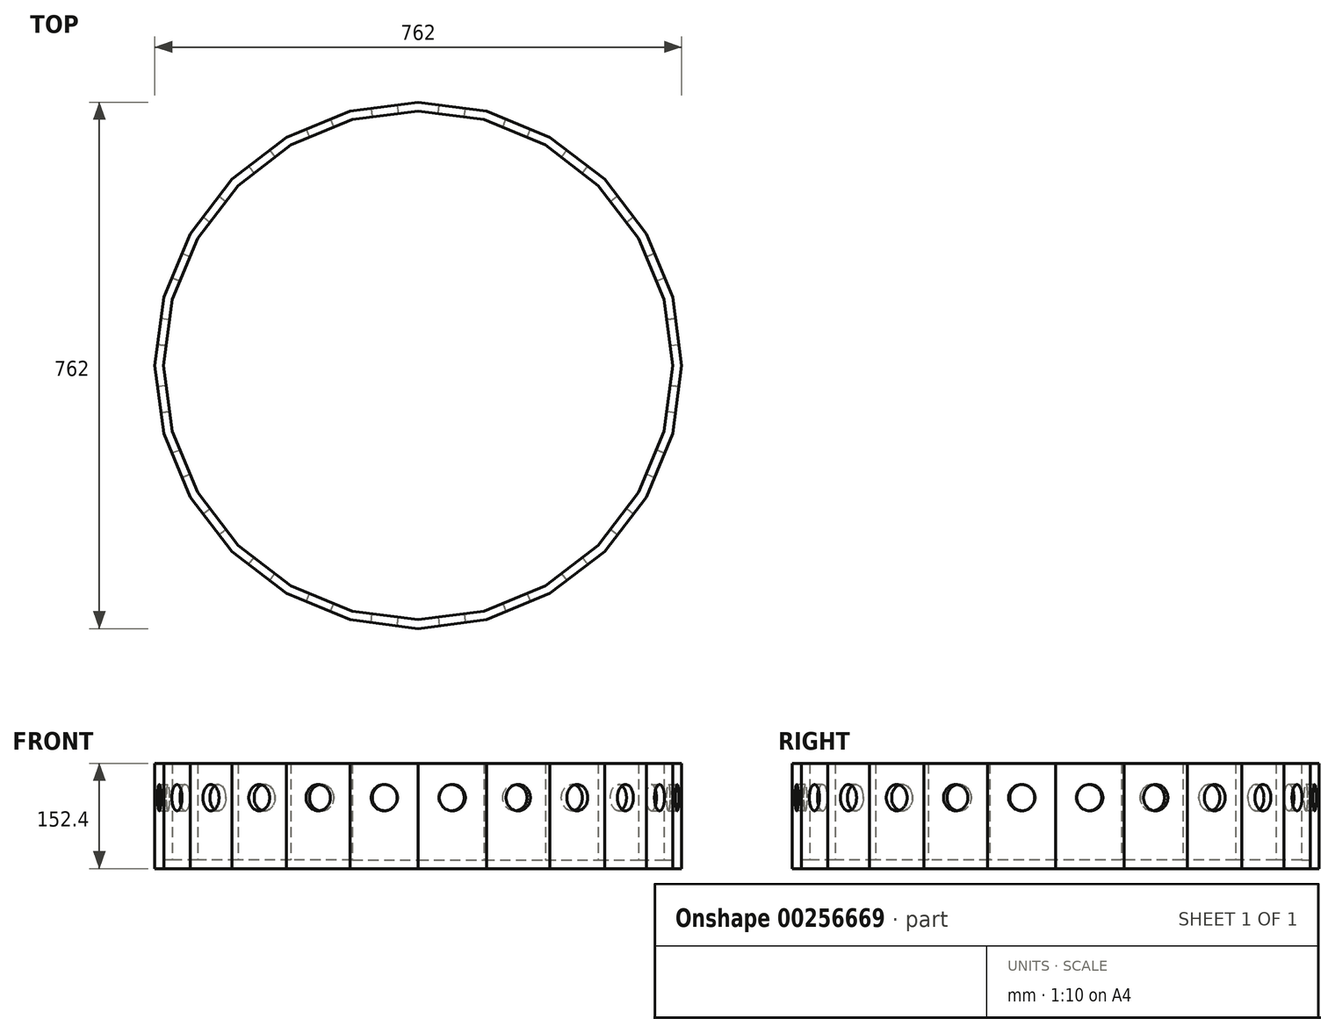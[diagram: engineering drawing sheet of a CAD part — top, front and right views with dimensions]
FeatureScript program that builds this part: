
annotation { "Feature Type Name" : "Feature", "Feature Type Description" : "" }
export const myFeature = defineFeature(function(context is Context, id is Id, definition is map)
    precondition{}
    {
        {
            var Q0;
            Q0=qCreatedBy(makeId("Top.planeOp"),FACE);
            var sketch = newSketch(context, id + "F0", { "sketchPlane" : qUnion([Q0])});
            skCircle(sketch, "E0.cCircle", {"center": v(0, 0) * mm, "radius": 381 * mm, "construction": true});
            skLineSegment(sketch, "E0.0", {"start": v(0, 381) * mm, "end": v(98.61, 368.02) * mm});
            skLineSegment(sketch, "E0.1", {"start": v(98.61, 368.02) * mm, "end": v(190.5, 329.96) * mm});
            skLineSegment(sketch, "E0.2", {"start": v(190.5, 329.96) * mm, "end": v(269.4, 269.4) * mm});
            skLineSegment(sketch, "E0.3", {"start": v(269.4, 269.4) * mm, "end": v(329.96, 190.5) * mm});
            skLineSegment(sketch, "E0.4", {"start": v(329.96, 190.5) * mm, "end": v(368.02, 98.61) * mm});
            skLineSegment(sketch, "E0.5", {"start": v(368.02, 98.61) * mm, "end": v(381, 0) * mm});
            skLineSegment(sketch, "E0.6", {"start": v(381, 0) * mm, "end": v(368.02, -98.61) * mm});
            skLineSegment(sketch, "E0.7", {"start": v(368.02, -98.61) * mm, "end": v(329.96, -190.5) * mm});
            skLineSegment(sketch, "E0.8", {"start": v(329.96, -190.5) * mm, "end": v(269.4, -269.4) * mm});
            skLineSegment(sketch, "E0.9", {"start": v(269.4, -269.4) * mm, "end": v(190.5, -329.96) * mm});
            skLineSegment(sketch, "E0.10", {"start": v(190.5, -329.96) * mm, "end": v(98.61, -368.02) * mm});
            skLineSegment(sketch, "E0.11", {"start": v(98.61, -368.02) * mm, "end": v(0, -381) * mm});
            skLineSegment(sketch, "E0.12", {"start": v(0, -381) * mm, "end": v(-98.61, -368.02) * mm});
            skLineSegment(sketch, "E0.13", {"start": v(-98.61, -368.02) * mm, "end": v(-190.5, -329.96) * mm});
            skLineSegment(sketch, "E0.14", {"start": v(-190.5, -329.96) * mm, "end": v(-269.4, -269.4) * mm});
            skLineSegment(sketch, "E0.15", {"start": v(-269.4, -269.4) * mm, "end": v(-329.96, -190.5) * mm});
            skLineSegment(sketch, "E0.16", {"start": v(-329.96, -190.5) * mm, "end": v(-368.02, -98.61) * mm});
            skLineSegment(sketch, "E0.17", {"start": v(-368.02, -98.61) * mm, "end": v(-381, 0) * mm});
            skLineSegment(sketch, "E0.18", {"start": v(-381, 0) * mm, "end": v(-368.02, 98.61) * mm});
            skLineSegment(sketch, "E0.19", {"start": v(-368.02, 98.61) * mm, "end": v(-329.96, 190.5) * mm});
            skLineSegment(sketch, "E0.20", {"start": v(-329.96, 190.5) * mm, "end": v(-269.4, 269.4) * mm});
            skLineSegment(sketch, "E0.21", {"start": v(-269.4, 269.4) * mm, "end": v(-190.5, 329.96) * mm});
            skLineSegment(sketch, "E0.22", {"start": v(-190.5, 329.96) * mm, "end": v(-98.61, 368.02) * mm});
            skLineSegment(sketch, "E0.23", {"start": v(-98.61, 368.02) * mm, "end": v(0, 381) * mm});
            skCircle(sketch, "E1.cCircle", {"center": v(0, 0) * mm, "radius": 368.2 * mm, "construction": true});
            skLineSegment(sketch, "E1.0", {"start": v(0, 368.2) * mm, "end": v(95.3, 355.64) * mm});
            skLineSegment(sketch, "E1.1", {"start": v(95.3, 355.64) * mm, "end": v(184.1, 318.86) * mm});
            skLineSegment(sketch, "E1.2", {"start": v(184.1, 318.86) * mm, "end": v(260.35, 260.35) * mm});
            skLineSegment(sketch, "E1.3", {"start": v(260.35, 260.35) * mm, "end": v(318.86, 184.1) * mm});
            skLineSegment(sketch, "E1.4", {"start": v(318.86, 184.1) * mm, "end": v(355.64, 95.3) * mm});
            skLineSegment(sketch, "E1.5", {"start": v(355.64, 95.3) * mm, "end": v(368.2, 0) * mm});
            skLineSegment(sketch, "E1.6", {"start": v(368.2, 0) * mm, "end": v(355.64, -95.3) * mm});
            skLineSegment(sketch, "E1.7", {"start": v(355.64, -95.3) * mm, "end": v(318.86, -184.1) * mm});
            skLineSegment(sketch, "E1.8", {"start": v(318.86, -184.1) * mm, "end": v(260.35, -260.35) * mm});
            skLineSegment(sketch, "E1.9", {"start": v(260.35, -260.35) * mm, "end": v(184.1, -318.86) * mm});
            skLineSegment(sketch, "E1.10", {"start": v(184.1, -318.86) * mm, "end": v(95.3, -355.64) * mm});
            skLineSegment(sketch, "E1.11", {"start": v(95.3, -355.64) * mm, "end": v(0, -368.2) * mm});
            skLineSegment(sketch, "E1.12", {"start": v(0, -368.2) * mm, "end": v(-95.3, -355.64) * mm});
            skLineSegment(sketch, "E1.13", {"start": v(-95.3, -355.64) * mm, "end": v(-184.1, -318.86) * mm});
            skLineSegment(sketch, "E1.14", {"start": v(-184.1, -318.86) * mm, "end": v(-260.35, -260.35) * mm});
            skLineSegment(sketch, "E1.15", {"start": v(-260.35, -260.35) * mm, "end": v(-318.86, -184.1) * mm});
            skLineSegment(sketch, "E1.16", {"start": v(-318.86, -184.1) * mm, "end": v(-355.64, -95.3) * mm});
            skLineSegment(sketch, "E1.17", {"start": v(-355.64, -95.3) * mm, "end": v(-368.2, 0) * mm});
            skLineSegment(sketch, "E1.18", {"start": v(-368.2, 0) * mm, "end": v(-355.64, 95.3) * mm});
            skLineSegment(sketch, "E1.19", {"start": v(-355.64, 95.3) * mm, "end": v(-318.86, 184.1) * mm});
            skLineSegment(sketch, "E1.20", {"start": v(-318.86, 184.1) * mm, "end": v(-260.35, 260.35) * mm});
            skLineSegment(sketch, "E1.21", {"start": v(-260.35, 260.35) * mm, "end": v(-184.1, 318.86) * mm});
            skLineSegment(sketch, "E1.22", {"start": v(-184.1, 318.86) * mm, "end": v(-95.3, 355.64) * mm});
            skLineSegment(sketch, "E1.23", {"start": v(-95.3, 355.64) * mm, "end": v(0, 368.2) * mm});
            skSolve(sketch);
        }
        {
            var Q0;
            Q0=makeQuery(id+"F0.imprint","IMPRINT",FACE,{"disambiguationData":[TD([[makeQuery(id+"F0.imprint","IMPRINT",EDGE,{"derivedFrom":sQuery(id+"F0.wireOp",EDGE,"E0.0")}),-1.0]])]});
            extrude(context, id + "F1", {"entities" : qUnion([Q0]), "depth" : 152.4 * mm});
        }
        {
            var Q0;
            Q0=makeQuery(id+"F0.imprint","IMPRINT",FACE,{"disambiguationData":[TD([[makeQuery(id+"F0.imprint","IMPRINT",EDGE,{"derivedFrom":sQuery(id+"F0.wireOp",EDGE,"E1.0")}),-1.0]])]});
            extrude(context, id + "F2", {"entities" : qUnion([Q0]), "operationType" : NewBodyOperationType.ADD, "depth" : 12.7 * mm});
        }
        {
            var Q0;
            Q0=makeQuery(id+"F1.opExtrude","SWEPT_FACE",FACE,{"disambiguationData":[OSD([sQuery(id+"F0.wireOp",EDGE,"E0.11")])]});
            var sketch = newSketch(context, id + "F3", { "sketchPlane" : qUnion([Q0])});
            skLineSegment(sketch, "E2.bottom", {"start": v(-49.73, 152.4) * mm, "end": v(49.73, 152.4) * mm});
            skLineSegment(sketch, "E2.top", {"start": v(-49.73, 52.94) * mm, "end": v(49.73, 52.94) * mm});
            skLineSegment(sketch, "E2.left", {"start": v(-49.73, 152.4) * mm, "end": v(-49.73, 52.94) * mm});
            skLineSegment(sketch, "E2.right", {"start": v(49.73, 152.4) * mm, "end": v(49.73, 52.94) * mm});
            skLineSegment(sketch, "E3", {"start": v(-49.73, 152.4) * mm, "end": v(49.73, 52.94) * mm});
            skPoint(sketch, "E4", {"position": v(0, 102.67) * mm});
            skSolve(sketch);
        }
        {
            var Q0;
            Q0=makeQuery(id+"F1.opExtrude","SWEPT_FACE",FACE,{"disambiguationData":[OSD([sQuery(id+"F0.wireOp",EDGE,"E0.10")])]});
            var sketch = newSketch(context, id + "F4", { "sketchPlane" : qUnion([Q0])});
            skLineSegment(sketch, "E5.bottom", {"start": v(-49.73, 152.4) * mm, "end": v(49.73, 152.4) * mm});
            skLineSegment(sketch, "E5.top", {"start": v(-49.73, 52.94) * mm, "end": v(49.73, 52.94) * mm});
            skLineSegment(sketch, "E5.left", {"start": v(-49.73, 152.4) * mm, "end": v(-49.73, 52.94) * mm});
            skLineSegment(sketch, "E5.right", {"start": v(49.73, 152.4) * mm, "end": v(49.73, 52.94) * mm});
            skLineSegment(sketch, "E6", {"start": v(-49.73, 152.4) * mm, "end": v(49.73, 52.94) * mm});
            skPoint(sketch, "E7", {"position": v(0, 102.67) * mm});
            skSolve(sketch);
        }
        {
            var Q0;
            Q0=makeQuery(id+"F1.opExtrude","SWEPT_FACE",FACE,{"disambiguationData":[OSD([sQuery(id+"F0.wireOp",EDGE,"E0.9")])]});
            var sketch = newSketch(context, id + "F5", { "sketchPlane" : qUnion([Q0])});
            skLineSegment(sketch, "E8.bottom", {"start": v(-49.73, 152.4) * mm, "end": v(49.73, 152.4) * mm});
            skLineSegment(sketch, "E8.top", {"start": v(-49.73, 52.94) * mm, "end": v(49.73, 52.94) * mm});
            skLineSegment(sketch, "E8.left", {"start": v(-49.73, 152.4) * mm, "end": v(-49.73, 52.94) * mm});
            skLineSegment(sketch, "E8.right", {"start": v(49.73, 152.4) * mm, "end": v(49.73, 52.94) * mm});
            skLineSegment(sketch, "E9", {"start": v(-49.73, 152.4) * mm, "end": v(49.73, 52.94) * mm});
            skPoint(sketch, "E10", {"position": v(0, 102.67) * mm});
            skSolve(sketch);
        }
        {
            var Q0;
            Q0=makeQuery(id+"F1.opExtrude","SWEPT_FACE",FACE,{"disambiguationData":[OSD([sQuery(id+"F0.wireOp",EDGE,"E0.8")])]});
            var sketch = newSketch(context, id + "F6", { "sketchPlane" : qUnion([Q0])});
            skLineSegment(sketch, "E11.bottom", {"start": v(-49.73, 152.4) * mm, "end": v(49.73, 152.4) * mm});
            skLineSegment(sketch, "E11.top", {"start": v(-49.73, 52.94) * mm, "end": v(49.73, 52.94) * mm});
            skLineSegment(sketch, "E11.left", {"start": v(-49.73, 152.4) * mm, "end": v(-49.73, 52.94) * mm});
            skLineSegment(sketch, "E11.right", {"start": v(49.73, 152.4) * mm, "end": v(49.73, 52.94) * mm});
            skLineSegment(sketch, "E12", {"start": v(-49.73, 152.4) * mm, "end": v(49.73, 52.94) * mm});
            skPoint(sketch, "E13", {"position": v(0, 102.67) * mm});
            skSolve(sketch);
        }
        {
            var Q0;
            Q0=makeQuery(id+"F1.opExtrude","SWEPT_FACE",FACE,{"disambiguationData":[OSD([sQuery(id+"F0.wireOp",EDGE,"E0.7")])]});
            var sketch = newSketch(context, id + "F7", { "sketchPlane" : qUnion([Q0])});
            skLineSegment(sketch, "E14.bottom", {"start": v(-49.73, 152.4) * mm, "end": v(49.73, 152.4) * mm});
            skLineSegment(sketch, "E14.top", {"start": v(-49.73, 52.94) * mm, "end": v(49.73, 52.94) * mm});
            skLineSegment(sketch, "E14.left", {"start": v(-49.73, 152.4) * mm, "end": v(-49.73, 52.94) * mm});
            skLineSegment(sketch, "E14.right", {"start": v(49.73, 152.4) * mm, "end": v(49.73, 52.94) * mm});
            skLineSegment(sketch, "E15", {"start": v(-49.73, 152.4) * mm, "end": v(49.73, 52.94) * mm});
            skPoint(sketch, "E16", {"position": v(0, 102.67) * mm});
            skSolve(sketch);
        }
        {
            var Q0;
            Q0=makeQuery(id+"F1.opExtrude","SWEPT_FACE",FACE,{"disambiguationData":[OSD([sQuery(id+"F0.wireOp",EDGE,"E0.6")])]});
            var sketch = newSketch(context, id + "F8", { "sketchPlane" : qUnion([Q0])});
            skLineSegment(sketch, "E17.bottom", {"start": v(-49.73, 152.4) * mm, "end": v(49.73, 152.4) * mm});
            skLineSegment(sketch, "E17.top", {"start": v(-49.73, 52.94) * mm, "end": v(49.73, 52.94) * mm});
            skLineSegment(sketch, "E17.left", {"start": v(-49.73, 152.4) * mm, "end": v(-49.73, 52.94) * mm});
            skLineSegment(sketch, "E17.right", {"start": v(49.73, 152.4) * mm, "end": v(49.73, 52.94) * mm});
            skLineSegment(sketch, "E18", {"start": v(-49.73, 152.4) * mm, "end": v(49.73, 52.94) * mm});
            skPoint(sketch, "E19", {"position": v(0, 102.67) * mm});
            skSolve(sketch);
        }
        {
            var Q0;
            Q0=makeQuery(id+"F1.opExtrude","SWEPT_FACE",FACE,{"disambiguationData":[OSD([sQuery(id+"F0.wireOp",EDGE,"E0.5")])]});
            var sketch = newSketch(context, id + "F9", { "sketchPlane" : qUnion([Q0])});
            skLineSegment(sketch, "E20.bottom", {"start": v(-49.73, 152.4) * mm, "end": v(49.73, 152.4) * mm});
            skLineSegment(sketch, "E20.top", {"start": v(-49.73, 52.94) * mm, "end": v(49.73, 52.94) * mm});
            skLineSegment(sketch, "E20.left", {"start": v(-49.73, 152.4) * mm, "end": v(-49.73, 52.94) * mm});
            skLineSegment(sketch, "E20.right", {"start": v(49.73, 152.4) * mm, "end": v(49.73, 52.94) * mm});
            skLineSegment(sketch, "E21", {"start": v(-49.73, 152.4) * mm, "end": v(49.73, 52.94) * mm});
            skPoint(sketch, "E22", {"position": v(0, 102.67) * mm});
            skSolve(sketch);
        }
        {
            var Q0;
            Q0=makeQuery(id+"F1.opExtrude","SWEPT_FACE",FACE,{"disambiguationData":[OSD([sQuery(id+"F0.wireOp",EDGE,"E0.4")])]});
            var sketch = newSketch(context, id + "F10", { "sketchPlane" : qUnion([Q0])});
            skLineSegment(sketch, "E23.bottom", {"start": v(-49.73, 152.4) * mm, "end": v(49.73, 152.4) * mm});
            skLineSegment(sketch, "E23.top", {"start": v(-49.73, 52.94) * mm, "end": v(49.73, 52.94) * mm});
            skLineSegment(sketch, "E23.left", {"start": v(-49.73, 152.4) * mm, "end": v(-49.73, 52.94) * mm});
            skLineSegment(sketch, "E23.right", {"start": v(49.73, 152.4) * mm, "end": v(49.73, 52.94) * mm});
            skLineSegment(sketch, "E24", {"start": v(-49.73, 152.4) * mm, "end": v(49.73, 52.94) * mm});
            skPoint(sketch, "E25", {"position": v(0, 102.67) * mm});
            skSolve(sketch);
        }
        {
            var Q0;
            Q0=makeQuery(id+"F1.opExtrude","SWEPT_FACE",FACE,{"disambiguationData":[OSD([sQuery(id+"F0.wireOp",EDGE,"E0.3")])]});
            var sketch = newSketch(context, id + "F11", { "sketchPlane" : qUnion([Q0])});
            skLineSegment(sketch, "E26.bottom", {"start": v(-49.73, 152.4) * mm, "end": v(49.73, 152.4) * mm});
            skLineSegment(sketch, "E26.top", {"start": v(-49.73, 52.94) * mm, "end": v(49.73, 52.94) * mm});
            skLineSegment(sketch, "E26.left", {"start": v(-49.73, 152.4) * mm, "end": v(-49.73, 52.94) * mm});
            skLineSegment(sketch, "E26.right", {"start": v(49.73, 152.4) * mm, "end": v(49.73, 52.94) * mm});
            skLineSegment(sketch, "E27", {"start": v(-49.73, 152.4) * mm, "end": v(49.73, 52.94) * mm});
            skPoint(sketch, "E28", {"position": v(0, 102.67) * mm});
            skSolve(sketch);
        }
        {
            var Q0;
            Q0=makeQuery(id+"F1.opExtrude","SWEPT_FACE",FACE,{"disambiguationData":[OSD([sQuery(id+"F0.wireOp",EDGE,"E0.2")])]});
            var sketch = newSketch(context, id + "F12", { "sketchPlane" : qUnion([Q0])});
            skLineSegment(sketch, "E29.bottom", {"start": v(-49.73, 152.4) * mm, "end": v(49.73, 152.4) * mm});
            skLineSegment(sketch, "E29.top", {"start": v(-49.73, 52.94) * mm, "end": v(49.73, 52.94) * mm});
            skLineSegment(sketch, "E29.left", {"start": v(-49.73, 152.4) * mm, "end": v(-49.73, 52.94) * mm});
            skLineSegment(sketch, "E29.right", {"start": v(49.73, 152.4) * mm, "end": v(49.73, 52.94) * mm});
            skLineSegment(sketch, "E30", {"start": v(-49.73, 152.4) * mm, "end": v(49.73, 52.94) * mm});
            skPoint(sketch, "E31", {"position": v(0, 102.67) * mm});
            skSolve(sketch);
        }
        {
            var Q0;
            Q0=makeQuery(id+"F1.opExtrude","SWEPT_FACE",FACE,{"disambiguationData":[OSD([sQuery(id+"F0.wireOp",EDGE,"E0.1")])]});
            var sketch = newSketch(context, id + "F13", { "sketchPlane" : qUnion([Q0])});
            skLineSegment(sketch, "E32.bottom", {"start": v(-49.73, 152.4) * mm, "end": v(49.73, 152.4) * mm});
            skLineSegment(sketch, "E32.top", {"start": v(-49.73, 52.94) * mm, "end": v(49.73, 52.94) * mm});
            skLineSegment(sketch, "E32.left", {"start": v(-49.73, 152.4) * mm, "end": v(-49.73, 52.94) * mm});
            skLineSegment(sketch, "E32.right", {"start": v(49.73, 152.4) * mm, "end": v(49.73, 52.94) * mm});
            skLineSegment(sketch, "E33", {"start": v(-49.73, 152.4) * mm, "end": v(49.73, 52.94) * mm});
            skPoint(sketch, "E34", {"position": v(0, 102.67) * mm});
            skSolve(sketch);
        }
        {
            var Q0;
            Q0=makeQuery(id+"F1.opExtrude","SWEPT_FACE",FACE,{"disambiguationData":[OSD([sQuery(id+"F0.wireOp",EDGE,"E0.0")])]});
            var sketch = newSketch(context, id + "F14", { "sketchPlane" : qUnion([Q0])});
            skLineSegment(sketch, "E35.bottom", {"start": v(-49.73, 152.4) * mm, "end": v(49.73, 152.4) * mm});
            skLineSegment(sketch, "E35.top", {"start": v(-49.73, 52.94) * mm, "end": v(49.73, 52.94) * mm});
            skLineSegment(sketch, "E35.left", {"start": v(-49.73, 152.4) * mm, "end": v(-49.73, 52.94) * mm});
            skLineSegment(sketch, "E35.right", {"start": v(49.73, 152.4) * mm, "end": v(49.73, 52.94) * mm});
            skLineSegment(sketch, "E36", {"start": v(-49.73, 152.4) * mm, "end": v(49.73, 52.94) * mm});
            skPoint(sketch, "E37", {"position": v(0, 102.67) * mm});
            skSolve(sketch);
        }
        {
            var Q0;
            Q0=sQuery(id+"F14.wireOp",VERTEX,"E37");
            var Q1;
            Q1=sQuery(id+"F13.wireOp",VERTEX,"E34");
            var Q2;
            Q2=sQuery(id+"F12.wireOp",VERTEX,"E31");
            var Q3;
            Q3=sQuery(id+"F11.wireOp",VERTEX,"E28");
            var Q4;
            Q4=sQuery(id+"F10.wireOp",VERTEX,"E25");
            var Q5;
            Q5=sQuery(id+"F9.wireOp",VERTEX,"E22");
            var Q6;
            Q6=sQuery(id+"F8.wireOp",VERTEX,"E19");
            var Q7;
            Q7=sQuery(id+"F7.wireOp",VERTEX,"E16");
            var Q8;
            Q8=sQuery(id+"F6.wireOp",VERTEX,"E13");
            var Q9;
            Q9=sQuery(id+"F5.wireOp",VERTEX,"E10");
            var Q10;
            Q10=sQuery(id+"F4.wireOp",VERTEX,"E7");
            var Q11;
            Q11=sQuery(id+"F3.wireOp",VERTEX,"E4");
            var Q12;
            Q12=makeQuery(id+"F1.opExtrude","SWEPT_BODY",BODY,{"disambiguationData":[OSD([sQuery(id+"F0.wireOp",EDGE,"E0.0"),sQuery(id+"F0.wireOp",EDGE,"E0.1"),sQuery(id+"F0.wireOp",EDGE,"E0.2"),sQuery(id+"F0.wireOp",EDGE,"E0.3"),sQuery(id+"F0.wireOp",EDGE,"E0.4"),sQuery(id+"F0.wireOp",EDGE,"E0.5"),sQuery(id+"F0.wireOp",EDGE,"E0.6"),sQuery(id+"F0.wireOp",EDGE,"E0.7"),sQuery(id+"F0.wireOp",EDGE,"E0.8"),sQuery(id+"F0.wireOp",EDGE,"E0.9"),sQuery(id+"F0.wireOp",EDGE,"E0.10"),sQuery(id+"F0.wireOp",EDGE,"E0.11"),sQuery(id+"F0.wireOp",EDGE,"E0.12"),sQuery(id+"F0.wireOp",EDGE,"E0.13"),sQuery(id+"F0.wireOp",EDGE,"E0.14"),sQuery(id+"F0.wireOp",EDGE,"E0.15"),sQuery(id+"F0.wireOp",EDGE,"E0.16"),sQuery(id+"F0.wireOp",EDGE,"E0.17"),sQuery(id+"F0.wireOp",EDGE,"E0.18"),sQuery(id+"F0.wireOp",EDGE,"E0.19"),sQuery(id+"F0.wireOp",EDGE,"E0.20"),sQuery(id+"F0.wireOp",EDGE,"E0.21"),sQuery(id+"F0.wireOp",EDGE,"E0.22"),sQuery(id+"F0.wireOp",EDGE,"E0.23"),sQuery(id+"F0.wireOp",EDGE,"8IWwi9vk-1Jyi-8dIN-RrB3-AOC0VOCXxqhx")])]});
            hole(context, id + "F15", {"style" : HoleStyle.SIMPLE, "endStyle" : HoleEndStyle.THROUGH, "holeDiameter" : 38.1 * mm, "tappedDepth" : 12.7 * mm, "tapClearance" : 3, "locations" : qUnion([Q0, Q1, Q2, Q3, Q4, Q5, Q6, Q7, Q8, Q9, Q10, Q11]), "scope" : qUnion([Q12])});
        }
    });
